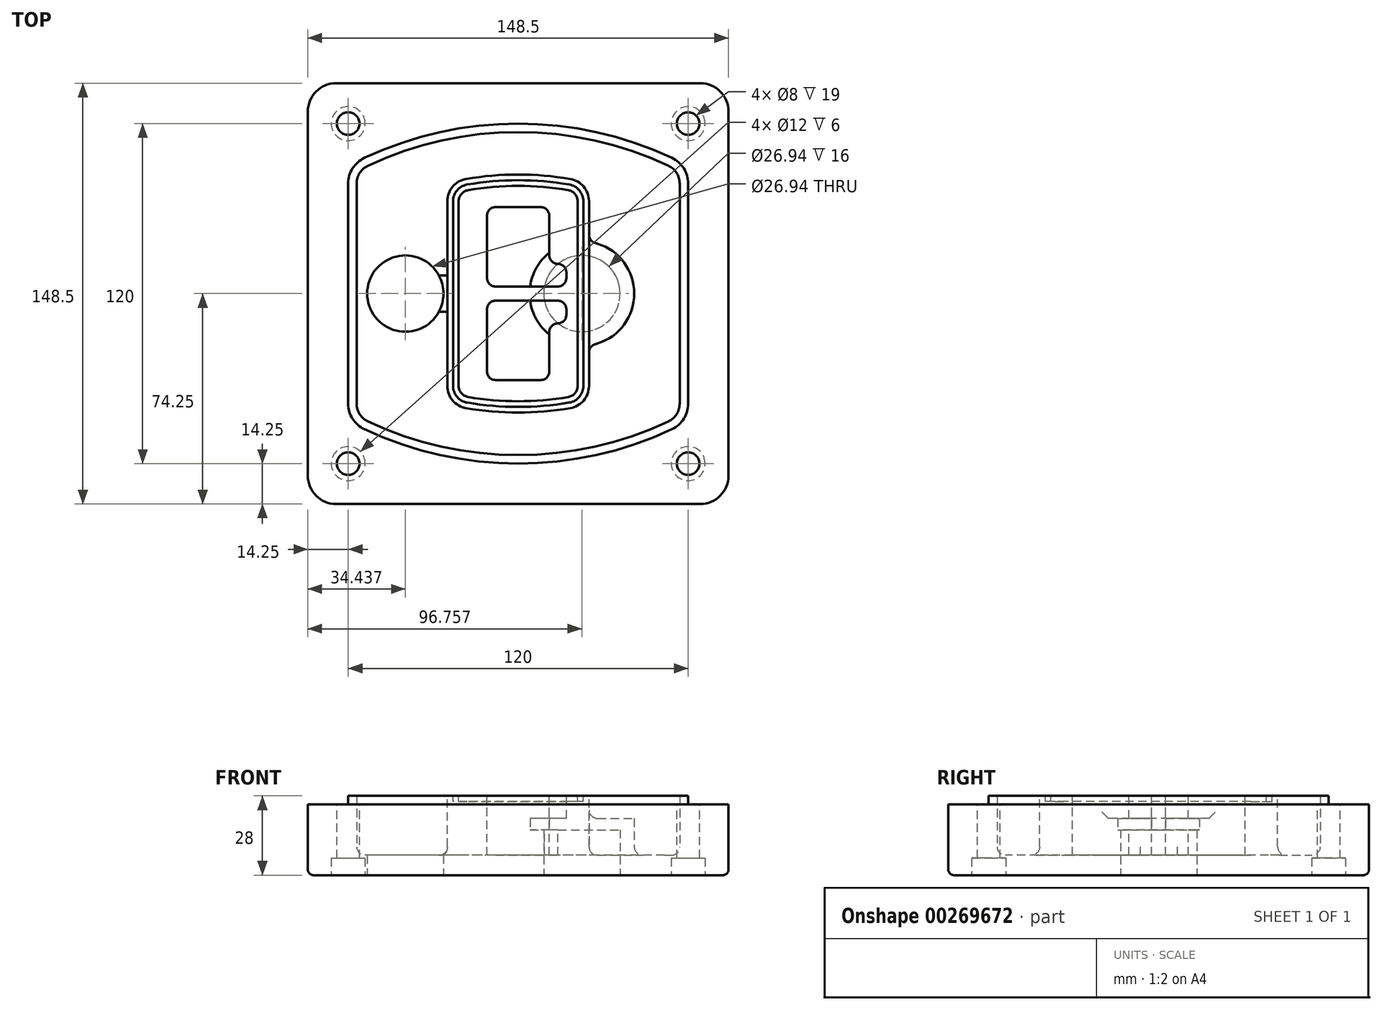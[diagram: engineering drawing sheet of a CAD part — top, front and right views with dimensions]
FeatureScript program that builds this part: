
annotation { "Feature Type Name" : "Feature", "Feature Type Description" : "" }
export const myFeature = defineFeature(function(context is Context, id is Id, definition is map)
    precondition{}
    {
        {
            var Q0;
            Q0=qCreatedBy(makeId("Top.planeOp"),FACE);
            var sketch = newSketch(context, id + "F0", { "sketchPlane" : qUnion([Q0])});
            skPoint(sketch, "E0.rect.middle", {"position": v(0, 0) * mm});
            skLineSegment(sketch, "E1.bottom", {"start": v(-64.25, -74.25) * mm, "end": v(64.25, -74.25) * mm});
            skLineSegment(sketch, "E1.top", {"start": v(-64.25, 74.25) * mm, "end": v(64.25, 74.25) * mm});
            skLineSegment(sketch, "E1.left", {"start": v(-74.25, -64.25) * mm, "end": v(-74.25, 64.25) * mm});
            skLineSegment(sketch, "E1.right", {"start": v(74.25, -64.25) * mm, "end": v(74.25, 64.25) * mm});
            skLineSegment(sketch, "E2", {"start": v(-74.25, 74.25) * mm, "end": v(74.25, -74.25) * mm, "construction": true});
            skLineSegment(sketch, "E3", {"start": v(74.25, 74.25) * mm, "end": v(-74.25, -74.25) * mm, "construction": true});
            skCircle(sketch, "E4", {"center": v(-60, 60) * mm, "radius": 4 * mm});
            skCircle(sketch, "E5", {"center": v(60, 60) * mm, "radius": 4 * mm});
            skCircle(sketch, "E6", {"center": v(60, -60) * mm, "radius": 4 * mm});
            skCircle(sketch, "E7", {"center": v(-60, -60) * mm, "radius": 4 * mm});
            skLineSegment(sketch, "E8", {"start": v(-60, 60) * mm, "end": v(60, 60) * mm, "construction": true});
            skLineSegment(sketch, "E9", {"start": v(60, 60) * mm, "end": v(60, -60) * mm, "construction": true});
            skLineSegment(sketch, "E10", {"start": v(60, -60) * mm, "end": v(-60, -60) * mm, "construction": true});
            skLineSegment(sketch, "E11", {"start": v(-60, -60) * mm, "end": v(-60, 60) * mm, "construction": true});
            skLineSegment(sketch, "E12", {"start": v(-60, 38.83) * mm, "end": v(-60, -38.83) * mm});
            skLineSegment(sketch, "E13", {"start": v(60, 38.83) * mm, "end": v(60, -38.83) * mm});
            skArc(sketch, "E14", {"start": v(54.26, 47.88) * mm, "mid": v(0, 60) * mm, "end": v(-54.26, 47.88) * mm});
            skArc(sketch, "E15", {"start": v(-54.26, -47.88) * mm, "mid": v(0, -60) * mm, "end": v(54.26, -47.88) * mm});
            skLineSegment(sketch, "E16", {"start": v(-60, 0) * mm, "end": v(60, 0) * mm, "construction": true});
            skPoint(sketch, "E17.visualSharp", {"position": v(-60, -45) * mm});
            skArc(sketch, "E17.filletArc", {"start": v(-60, -38.83) * mm, "mid": v(-58.44, -44.2) * mm, "end": v(-54.26, -47.88) * mm});
            skPoint(sketch, "E18.visualSharp", {"position": v(-60, 45) * mm});
            skArc(sketch, "E18.filletArc", {"start": v(-54.26, 47.88) * mm, "mid": v(-58.44, 44.2) * mm, "end": v(-60, 38.83) * mm});
            skPoint(sketch, "E19.visualSharp", {"position": v(60, 45) * mm});
            skArc(sketch, "E19.filletArc", {"start": v(60, 38.83) * mm, "mid": v(58.44, 44.2) * mm, "end": v(54.26, 47.88) * mm});
            skPoint(sketch, "E20.visualSharp", {"position": v(60, -45) * mm});
            skArc(sketch, "E20.filletArc", {"start": v(54.26, -47.88) * mm, "mid": v(58.44, -44.2) * mm, "end": v(60, -38.83) * mm});
            skPoint(sketch, "E21.visualSharp", {"position": v(-74.25, 74.25) * mm});
            skArc(sketch, "E21.filletArc", {"start": v(-64.25, 74.25) * mm, "mid": v(-71.32, 71.32) * mm, "end": v(-74.25, 64.25) * mm});
            skPoint(sketch, "E22.visualSharp", {"position": v(74.25, 74.25) * mm});
            skArc(sketch, "E22.filletArc", {"start": v(74.25, 64.25) * mm, "mid": v(71.32, 71.32) * mm, "end": v(64.25, 74.25) * mm});
            skPoint(sketch, "E23.visualSharp", {"position": v(74.25, -74.25) * mm});
            skArc(sketch, "E23.filletArc", {"start": v(64.25, -74.25) * mm, "mid": v(71.32, -71.32) * mm, "end": v(74.25, -64.25) * mm});
            skPoint(sketch, "E24.visualSharp", {"position": v(-74.25, -74.25) * mm});
            skArc(sketch, "E24.filletArc", {"start": v(-74.25, -64.25) * mm, "mid": v(-71.32, -71.32) * mm, "end": v(-64.25, -74.25) * mm});
            skArc(sketch, "E25.0", {"start": v(57, 38.83) * mm, "mid": v(55.9, 42.58) * mm, "end": v(52.98, 45.17) * mm});
            skLineSegment(sketch, "E25.1", {"start": v(57, 38.83) * mm, "end": v(57, -38.83) * mm});
            skArc(sketch, "E25.2", {"start": v(52.98, -45.17) * mm, "mid": v(55.9, -42.58) * mm, "end": v(57, -38.83) * mm});
            skArc(sketch, "E25.3", {"start": v(-52.98, -45.17) * mm, "mid": v(0, -57) * mm, "end": v(52.98, -45.17) * mm});
            skArc(sketch, "E25.4", {"start": v(-57, -38.83) * mm, "mid": v(-55.9, -42.58) * mm, "end": v(-52.98, -45.17) * mm});
            skArc(sketch, "E25.5", {"start": v(52.98, 45.17) * mm, "mid": v(0, 57) * mm, "end": v(-52.98, 45.17) * mm});
            skLineSegment(sketch, "E25.6", {"start": v(-57, 38.83) * mm, "end": v(-57, -38.83) * mm});
            skArc(sketch, "E25.7", {"start": v(-52.98, 45.17) * mm, "mid": v(-55.9, 42.58) * mm, "end": v(-57, 38.83) * mm});
            skArc(sketch, "E26.0", {"start": v(-55.96, 51.5) * mm, "mid": v(-61.82, 46.33) * mm, "end": v(-64, 38.83) * mm});
            skArc(sketch, "E26.1", {"start": v(55.96, 51.5) * mm, "mid": v(0, 64) * mm, "end": v(-55.96, 51.5) * mm});
            skArc(sketch, "E26.2", {"start": v(64, 38.83) * mm, "mid": v(61.82, 46.33) * mm, "end": v(55.96, 51.5) * mm});
            skLineSegment(sketch, "E26.3", {"start": v(64, 38.83) * mm, "end": v(64, -38.83) * mm});
            skArc(sketch, "E26.4", {"start": v(55.96, -51.5) * mm, "mid": v(61.82, -46.33) * mm, "end": v(64, -38.83) * mm});
            skLineSegment(sketch, "E26.5", {"start": v(-64, 38.83) * mm, "end": v(-64, -38.83) * mm});
            skArc(sketch, "E26.6", {"start": v(-55.96, -51.5) * mm, "mid": v(0, -64) * mm, "end": v(55.96, -51.5) * mm});
            skArc(sketch, "E26.7", {"start": v(-64, -38.83) * mm, "mid": v(-61.82, -46.33) * mm, "end": v(-55.96, -51.5) * mm});
            skSolve(sketch);
        }
        {
            var Q0;
            Q0=makeQuery(id+"F0.imprint","IMPRINT",FACE,{"disambiguationData":[TD([[makeQuery(id+"F0.imprint","IMPRINT",EDGE,{"derivedFrom":sQuery(id+"F0.wireOp",EDGE,"E1.bottom")}),1.0]])]});
            var Q1;
            Q1=makeQuery(id+"F0.imprint","IMPRINT",FACE,{"disambiguationData":[TD([[makeQuery(id+"F0.imprint","IMPRINT",EDGE,{"derivedFrom":sQuery(id+"F0.wireOp",EDGE,"E12")}),1.0]])]});
            var Q2;
            Q2=makeQuery(id+"F0.imprint","IMPRINT",FACE,{"disambiguationData":[TD([[makeQuery(id+"F0.imprint","IMPRINT",EDGE,{"derivedFrom":sQuery(id+"F0.wireOp",EDGE,"E25.0")}),1.0]])]});
            var Q3;
            Q3=makeQuery(id+"F0.imprint","IMPRINT",FACE,{"disambiguationData":[TD([[makeQuery(id+"F0.imprint","IMPRINT",EDGE,{"derivedFrom":sQuery(id+"F0.wireOp",EDGE,"E12")}),-1.0]])]});
            extrude(context, id + "F1", {"entities" : qUnion([Q0, Q1, Q2, Q3]), "oppositeDirection" : true, "depth" : 25 * mm});
        }
        {
            var Q0;
            Q0=makeQuery(id+"F0.imprint","IMPRINT",FACE,{"disambiguationData":[TD([[makeQuery(id+"F0.imprint","IMPRINT",EDGE,{"derivedFrom":sQuery(id+"F0.wireOp",EDGE,"E12")}),1.0]])]});
            extrude(context, id + "F2", {"entities" : qUnion([Q0]), "operationType" : NewBodyOperationType.ADD, "depth" : 3 * mm});
        }
        {
            var Q0;
            Q0=makeQuery(id+"F0.imprint","IMPRINT",FACE,{"disambiguationData":[TD([[makeQuery(id+"F0.imprint","IMPRINT",EDGE,{"derivedFrom":sQuery(id+"F0.wireOp",EDGE,"E25.0")}),1.0]])]});
            extrude(context, id + "F3", {"entities" : qUnion([Q0]), "operationType" : NewBodyOperationType.REMOVE, "oppositeDirection" : true, "depth" : 18 * mm});
        }
        {
            var Q0;
            Q0=makeQuery(id+"F2.opExtrude","CAP_FACE",FACE,{"disambiguationData":[OSD([sQuery(id+"F0.wireOp",EDGE,"E12"),sQuery(id+"F0.wireOp",EDGE,"E13"),sQuery(id+"F0.wireOp",EDGE,"E14"),sQuery(id+"F0.wireOp",EDGE,"E15"),sQuery(id+"F0.wireOp",EDGE,"E17.filletArc"),sQuery(id+"F0.wireOp",EDGE,"E18.filletArc"),sQuery(id+"F0.wireOp",EDGE,"E19.filletArc"),sQuery(id+"F0.wireOp",EDGE,"E20.filletArc"),sQuery(id+"F0.wireOp",EDGE,"E25.0"),sQuery(id+"F0.wireOp",EDGE,"E25.1"),sQuery(id+"F0.wireOp",EDGE,"E25.2"),sQuery(id+"F0.wireOp",EDGE,"E25.3"),sQuery(id+"F0.wireOp",EDGE,"E25.4"),sQuery(id+"F0.wireOp",EDGE,"E25.5"),sQuery(id+"F0.wireOp",EDGE,"E25.6"),sQuery(id+"F0.wireOp",EDGE,"E25.7")])],"isStart":false});
            var sketch = newSketch(context, id + "F4", { "sketchPlane" : qUnion([Q0])});
            skArc(sketch, "E27.0", {"start": v(-18.34, -40.45) * mm, "mid": v(0, -42) * mm, "end": v(18.34, -40.45) * mm});
            skArc(sketch, "E28.0", {"start": v(18.34, 40.45) * mm, "mid": v(0, 42) * mm, "end": v(-18.34, 40.45) * mm});
            skLineSegment(sketch, "E29", {"start": v(-25, 32.57) * mm, "end": v(-25, -32.57) * mm});
            skLineSegment(sketch, "E30", {"start": v(25, 32.57) * mm, "end": v(25, -32.57) * mm});
            skLineSegment(sketch, "E31", {"start": v(-25, 39.1) * mm, "end": v(25, 39.1) * mm, "construction": true});
            skLineSegment(sketch, "E32", {"start": v(-25, -39.1) * mm, "end": v(25, -39.1) * mm, "construction": true});
            skPoint(sketch, "E33.visualSharp", {"position": v(-25, 39.1) * mm});
            skArc(sketch, "E33.filletArc", {"start": v(-18.34, 40.45) * mm, "mid": v(-23.11, 37.73) * mm, "end": v(-25, 32.57) * mm});
            skPoint(sketch, "E34.visualSharp", {"position": v(25, 39.1) * mm});
            skArc(sketch, "E34.filletArc", {"start": v(25, 32.57) * mm, "mid": v(23.11, 37.73) * mm, "end": v(18.34, 40.45) * mm});
            skPoint(sketch, "E35.visualSharp", {"position": v(25, -39.1) * mm});
            skArc(sketch, "E35.filletArc", {"start": v(18.34, -40.45) * mm, "mid": v(23.11, -37.73) * mm, "end": v(25, -32.57) * mm});
            skPoint(sketch, "E36.visualSharp", {"position": v(-25, -39.1) * mm});
            skArc(sketch, "E36.filletArc", {"start": v(-25, -32.57) * mm, "mid": v(-23.11, -37.73) * mm, "end": v(-18.34, -40.45) * mm});
            skArc(sketch, "E37.0", {"start": v(52.98, 45.17) * mm, "mid": v(0, 57) * mm, "end": v(-52.98, 45.17) * mm});
            skArc(sketch, "E37.1", {"start": v(-52.98, 45.17) * mm, "mid": v(-55.9, 42.58) * mm, "end": v(-57, 38.83) * mm});
            skLineSegment(sketch, "E37.2", {"start": v(-57, 38.83) * mm, "end": v(-57, -38.83) * mm});
            skArc(sketch, "E37.3", {"start": v(-57, -38.83) * mm, "mid": v(-55.9, -42.58) * mm, "end": v(-52.98, -45.17) * mm});
            skArc(sketch, "E37.4", {"start": v(-52.98, -45.17) * mm, "mid": v(0, -57) * mm, "end": v(52.98, -45.17) * mm});
            skArc(sketch, "E37.5", {"start": v(52.98, -45.17) * mm, "mid": v(55.9, -42.58) * mm, "end": v(57, -38.83) * mm});
            skLineSegment(sketch, "E37.6", {"start": v(57, 38.83) * mm, "end": v(57, -38.83) * mm});
            skArc(sketch, "E37.7", {"start": v(57, 38.83) * mm, "mid": v(55.9, 42.58) * mm, "end": v(52.98, 45.17) * mm});
            skLineSegment(sketch, "E38.0", {"start": v(23, 32.57) * mm, "end": v(23, -32.57) * mm});
            skArc(sketch, "E38.1", {"start": v(18, -38.48) * mm, "mid": v(21.58, -36.44) * mm, "end": v(23, -32.57) * mm});
            skArc(sketch, "E38.2", {"start": v(-18, -38.48) * mm, "mid": v(0, -40) * mm, "end": v(18, -38.48) * mm});
            skArc(sketch, "E38.3", {"start": v(-23, -32.57) * mm, "mid": v(-21.58, -36.44) * mm, "end": v(-18, -38.48) * mm});
            skLineSegment(sketch, "E38.4", {"start": v(-23, 32.57) * mm, "end": v(-23, -32.57) * mm});
            skArc(sketch, "E38.5", {"start": v(23, 32.57) * mm, "mid": v(21.58, 36.44) * mm, "end": v(18, 38.48) * mm});
            skArc(sketch, "E38.6", {"start": v(-18, 38.48) * mm, "mid": v(-21.58, 36.44) * mm, "end": v(-23, 32.57) * mm});
            skArc(sketch, "E38.7", {"start": v(18, 38.48) * mm, "mid": v(0, 40) * mm, "end": v(-18, 38.48) * mm});
            skArc(sketch, "E39.0", {"start": v(21, 32.57) * mm, "mid": v(20.06, 35.15) * mm, "end": v(17.67, 36.5) * mm});
            skLineSegment(sketch, "E39.1", {"start": v(21, 32.57) * mm, "end": v(21, -32.57) * mm});
            skArc(sketch, "E39.2", {"start": v(17.67, -36.5) * mm, "mid": v(20.06, -35.15) * mm, "end": v(21, -32.57) * mm});
            skArc(sketch, "E39.3", {"start": v(-17.67, -36.5) * mm, "mid": v(0, -38) * mm, "end": v(17.67, -36.5) * mm});
            skArc(sketch, "E39.4", {"start": v(-21, -32.57) * mm, "mid": v(-20.06, -35.15) * mm, "end": v(-17.67, -36.5) * mm});
            skArc(sketch, "E39.5", {"start": v(17.67, 36.5) * mm, "mid": v(0, 38) * mm, "end": v(-17.67, 36.5) * mm});
            skLineSegment(sketch, "E39.6", {"start": v(-21, 32.57) * mm, "end": v(-21, -32.57) * mm});
            skArc(sketch, "E39.7", {"start": v(-17.67, 36.5) * mm, "mid": v(-20.06, 35.15) * mm, "end": v(-21, 32.57) * mm});
            skLineSegment(sketch, "E40", {"start": v(-25, 0) * mm, "end": v(25, 0) * mm, "construction": true});
            skLineSegment(sketch, "E41", {"start": v(-11, 5.5) * mm, "end": v(-11, 27.5) * mm});
            skLineSegment(sketch, "E42", {"start": v(-8, 30.5) * mm, "end": v(8, 30.5) * mm});
            skLineSegment(sketch, "E43", {"start": v(11, 27.5) * mm, "end": v(11, 13.5) * mm});
            skLineSegment(sketch, "E44", {"start": v(14, 10.5) * mm, "end": v(14, 10.5) * mm});
            skLineSegment(sketch, "E45", {"start": v(17, 7.5) * mm, "end": v(17, 5.5) * mm});
            skLineSegment(sketch, "E46", {"start": v(14, 2.5) * mm, "end": v(-8, 2.5) * mm});
            skPoint(sketch, "E47.visualSharp", {"position": v(-11, 30.5) * mm});
            skArc(sketch, "E47.filletArc", {"start": v(-8, 30.5) * mm, "mid": v(-10.12, 29.62) * mm, "end": v(-11, 27.5) * mm});
            skPoint(sketch, "E48.visualSharp", {"position": v(11, 30.5) * mm});
            skArc(sketch, "E48.filletArc", {"start": v(11, 27.5) * mm, "mid": v(10.12, 29.62) * mm, "end": v(8, 30.5) * mm});
            skPoint(sketch, "E49.visualSharp", {"position": v(11, 10.5) * mm});
            skArc(sketch, "E49.filletArc", {"start": v(11, 13.5) * mm, "mid": v(11.88, 11.38) * mm, "end": v(14, 10.5) * mm});
            skPoint(sketch, "E50.visualSharp", {"position": v(17, 10.5) * mm});
            skArc(sketch, "E50.filletArc", {"start": v(17, 7.5) * mm, "mid": v(16.12, 9.62) * mm, "end": v(14, 10.5) * mm});
            skPoint(sketch, "E51.visualSharp", {"position": v(17, 2.5) * mm});
            skArc(sketch, "E51.filletArc", {"start": v(14, 2.5) * mm, "mid": v(16.12, 3.38) * mm, "end": v(17, 5.5) * mm});
            skPoint(sketch, "E52.visualSharp", {"position": v(-11, 2.5) * mm});
            skArc(sketch, "E52.filletArc", {"start": v(-11, 5.5) * mm, "mid": v(-10.12, 3.38) * mm, "end": v(-8, 2.5) * mm});
            skLineSegment(sketch, "E53.0.MirrorCS", {"start": v(14, -2.5) * mm, "end": v(-8, -2.5) * mm});
            skArc(sketch, "E54.0.MirrorCS", {"start": v(-11, -5.5) * mm, "mid": v(-10.12, -3.38) * mm, "end": v(-8, -2.5) * mm});
            skLineSegment(sketch, "E55.0.MirrorCS", {"start": v(-11, -5.5) * mm, "end": v(-11, -27.5) * mm});
            skArc(sketch, "E56.0.MirrorCS", {"start": v(-8, -30.5) * mm, "mid": v(-10.12, -29.62) * mm, "end": v(-11, -27.5) * mm});
            skLineSegment(sketch, "E57.0.MirrorCS", {"start": v(-8, -30.5) * mm, "end": v(8, -30.5) * mm});
            skArc(sketch, "E58.0.MirrorCS", {"start": v(11, -27.5) * mm, "mid": v(10.12, -29.62) * mm, "end": v(8, -30.5) * mm});
            skLineSegment(sketch, "E59.0.MirrorCS", {"start": v(11, -27.5) * mm, "end": v(11, -13.5) * mm});
            skArc(sketch, "E60.0.MirrorCS", {"start": v(11, -13.5) * mm, "mid": v(11.88, -11.38) * mm, "end": v(14, -10.5) * mm});
            skArc(sketch, "E61.0.MirrorCS", {"start": v(17, -7.5) * mm, "mid": v(16.12, -9.62) * mm, "end": v(14, -10.5) * mm});
            skLineSegment(sketch, "E62.0.MirrorCS", {"start": v(17, -7.5) * mm, "end": v(17, -5.5) * mm});
            skArc(sketch, "E63.0.MirrorCS", {"start": v(14, -2.5) * mm, "mid": v(16.12, -3.38) * mm, "end": v(17, -5.5) * mm});
            skSolve(sketch);
        }
        {
            var Q0;
            Q0=makeQuery(id+"F4.imprint","IMPRINT",FACE,{"disambiguationData":[TD([[makeQuery(id+"F4.imprint","IMPRINT",EDGE,{"derivedFrom":sQuery(id+"F4.wireOp",EDGE,"E27.0")}),1.0]])]});
            var Q1;
            Q1=makeQuery(id+"F4.imprint","IMPRINT",FACE,{"disambiguationData":[TD([[makeQuery(id+"F4.imprint","IMPRINT",EDGE,{"derivedFrom":sQuery(id+"F4.wireOp",EDGE,"E38.0")}),-1.0]])]});
            var Q2;
            Q2=makeQuery(id+"F4.imprint","IMPRINT",FACE,{"disambiguationData":[TD([[makeQuery(id+"F4.imprint","IMPRINT",EDGE,{"derivedFrom":sQuery(id+"F4.wireOp",EDGE,"E39.0")}),1.0]])]});
            extrude(context, id + "F5", {"entities" : qUnion([Q0, Q1, Q2]), "operationType" : NewBodyOperationType.ADD, "endBound" : BoundingType.UP_TO_NEXT, "oppositeDirection" : true, "depth" : 25 * mm});
        }
        {
            var Q0;
            Q0=makeQuery(id+"F4.imprint","IMPRINT",FACE,{"disambiguationData":[TD([[makeQuery(id+"F4.imprint","IMPRINT",EDGE,{"derivedFrom":sQuery(id+"F4.wireOp",EDGE,"E38.0")}),-1.0]])]});
            extrude(context, id + "F6", {"entities" : qUnion([Q0]), "operationType" : NewBodyOperationType.REMOVE, "oppositeDirection" : true, "depth" : 2 * mm});
        }
        {
            var Q0;
            Q0=makeQuery(id+"F1.opExtrude","CAP_FACE",FACE,{"disambiguationData":[OSD([sQuery(id+"F0.wireOp",EDGE,"E1.bottom"),sQuery(id+"F0.wireOp",EDGE,"E1.top"),sQuery(id+"F0.wireOp",EDGE,"E1.left"),sQuery(id+"F0.wireOp",EDGE,"E1.right"),sQuery(id+"F0.wireOp",EDGE,"E4"),sQuery(id+"F0.wireOp",EDGE,"E5"),sQuery(id+"F0.wireOp",EDGE,"E6"),sQuery(id+"F0.wireOp",EDGE,"E7"),sQuery(id+"F0.wireOp",EDGE,"E21.filletArc"),sQuery(id+"F0.wireOp",EDGE,"E22.filletArc"),sQuery(id+"F0.wireOp",EDGE,"E23.filletArc"),sQuery(id+"F0.wireOp",EDGE,"E24.filletArc")])],"isStart":false});
            var sketch = newSketch(context, id + "F7", { "sketchPlane" : qUnion([Q0])});
            skCircle(sketch, "E64", {"center": v(22.5, 0) * mm, "radius": 13.47 * mm});
            skCircle(sketch, "E65", {"center": v(-39.81, 0) * mm, "radius": 13.47 * mm});
            skLineSegment(sketch, "E66", {"start": v(74.25, 0) * mm, "end": v(-74.25, 0) * mm});
            skCircle(sketch, "E67", {"center": v(22.5, 0) * mm, "radius": 18.47 * mm});
            skCircle(sketch, "E68", {"center": v(60, -60) * mm, "radius": 6 * mm});
            skCircle(sketch, "E69", {"center": v(-60, -60) * mm, "radius": 6 * mm});
            skCircle(sketch, "E70", {"center": v(-60, 60) * mm, "radius": 6 * mm});
            skCircle(sketch, "E71", {"center": v(60, 60) * mm, "radius": 6 * mm});
            skSolve(sketch);
        }
        {
            var Q0;
            {var subQ1=sQuery(id+"F7.wireOp",EDGE,"E66");var subQ4=sQuery(id+"F7.wireOp",EDGE,"E64");var subQ6=makeQuery(id+"F7.imprint","INTERSECT",VERTEX,{"disambiguationData":[OD(0.0)],"derivedFrom":[subQ4,subQ1]});Q0=makeQuery(id+"F7.imprint","IMPRINT",FACE,{"disambiguationData":[TD([[makeQuery(id+"F7.imprint","IMPRINT",EDGE,{"disambiguationData":[TD([[subQ6,-1.0]])],"derivedFrom":subQ4}),-1.0]])]});}
            var Q1;
            {var subQ0=sQuery(id+"F7.wireOp",EDGE,"E66");var subQ1=sQuery(id+"F7.wireOp",EDGE,"E64");var subQ3=makeQuery(id+"F7.imprint","INTERSECT",VERTEX,{"disambiguationData":[OD(0.0)],"derivedFrom":[subQ1,subQ0]});Q1=makeQuery(id+"F7.imprint","IMPRINT",FACE,{"disambiguationData":[TD([[makeQuery(id+"F7.imprint","IMPRINT",EDGE,{"disambiguationData":[TD([[subQ3,-1.0]])],"derivedFrom":subQ1}),1.0]])]});}
            var Q2;
            {var subQ0=sQuery(id+"F7.wireOp",EDGE,"E66");var subQ1=sQuery(id+"F7.wireOp",EDGE,"E64");var subQ3=makeQuery(id+"F7.imprint","INTERSECT",VERTEX,{"disambiguationData":[OD(0.0)],"derivedFrom":[subQ1,subQ0]});Q2=makeQuery(id+"F7.imprint","IMPRINT",FACE,{"disambiguationData":[TD([[makeQuery(id+"F7.imprint","IMPRINT",EDGE,{"disambiguationData":[TD([[subQ3,1.0]])],"derivedFrom":subQ1}),1.0]])]});}
            var Q3;
            {var subQ1=sQuery(id+"F7.wireOp",EDGE,"E66");var subQ4=sQuery(id+"F7.wireOp",EDGE,"E64");var subQ6=makeQuery(id+"F7.imprint","INTERSECT",VERTEX,{"disambiguationData":[OD(0.0)],"derivedFrom":[subQ4,subQ1]});Q3=makeQuery(id+"F7.imprint","IMPRINT",FACE,{"disambiguationData":[TD([[makeQuery(id+"F7.imprint","IMPRINT",EDGE,{"disambiguationData":[TD([[subQ6,1.0]])],"derivedFrom":subQ4}),-1.0]])]});}
            extrude(context, id + "F8", {"entities" : qUnion([Q0, Q1, Q2, Q3]), "operationType" : NewBodyOperationType.ADD, "oppositeDirection" : true, "depth" : 20 * mm});
        }
        {
            var Q0;
            {var subQ0=sQuery(id+"F7.wireOp",EDGE,"E66");var subQ1=sQuery(id+"F7.wireOp",EDGE,"E64");var subQ3=makeQuery(id+"F7.imprint","INTERSECT",VERTEX,{"disambiguationData":[OD(0.0)],"derivedFrom":[subQ1,subQ0]});Q0=makeQuery(id+"F7.imprint","IMPRINT",FACE,{"disambiguationData":[TD([[makeQuery(id+"F7.imprint","IMPRINT",EDGE,{"disambiguationData":[TD([[subQ3,-1.0]])],"derivedFrom":subQ1}),1.0]])]});}
            var Q1;
            {var subQ0=sQuery(id+"F7.wireOp",EDGE,"E66");var subQ1=sQuery(id+"F7.wireOp",EDGE,"E64");var subQ3=makeQuery(id+"F7.imprint","INTERSECT",VERTEX,{"disambiguationData":[OD(0.0)],"derivedFrom":[subQ1,subQ0]});Q1=makeQuery(id+"F7.imprint","IMPRINT",FACE,{"disambiguationData":[TD([[makeQuery(id+"F7.imprint","IMPRINT",EDGE,{"disambiguationData":[TD([[subQ3,1.0]])],"derivedFrom":subQ1}),1.0]])]});}
            extrude(context, id + "F9", {"entities" : qUnion([Q0, Q1]), "operationType" : NewBodyOperationType.REMOVE, "oppositeDirection" : true, "depth" : 16 * mm});
        }
        {
            var Q0;
            {var subQ0=sQuery(id+"F7.wireOp",EDGE,"E66");var subQ1=sQuery(id+"F7.wireOp",EDGE,"E65");var subQ3=makeQuery(id+"F7.imprint","INTERSECT",VERTEX,{"disambiguationData":[OD(0.0)],"derivedFrom":[subQ1,subQ0]});Q0=makeQuery(id+"F7.imprint","IMPRINT",FACE,{"disambiguationData":[TD([[makeQuery(id+"F7.imprint","IMPRINT",EDGE,{"disambiguationData":[TD([[subQ3,-1.0]])],"derivedFrom":subQ1}),1.0]])]});}
            var Q1;
            {var subQ0=sQuery(id+"F7.wireOp",EDGE,"E66");var subQ1=sQuery(id+"F7.wireOp",EDGE,"E65");var subQ3=makeQuery(id+"F7.imprint","INTERSECT",VERTEX,{"disambiguationData":[OD(0.0)],"derivedFrom":[subQ1,subQ0]});Q1=makeQuery(id+"F7.imprint","IMPRINT",FACE,{"disambiguationData":[TD([[makeQuery(id+"F7.imprint","IMPRINT",EDGE,{"disambiguationData":[TD([[subQ3,1.0]])],"derivedFrom":subQ1}),1.0]])]});}
            extrude(context, id + "F10", {"entities" : qUnion([Q0, Q1]), "operationType" : NewBodyOperationType.REMOVE, "oppositeDirection" : true, "depth" : 25 * mm});
        }
        {
            var Q0;
            Q0=makeQuery(id+"F7.imprint","IMPRINT",FACE,{"disambiguationData":[TD([[makeQuery(id+"F7.imprint","IMPRINT",EDGE,{"derivedFrom":sQuery(id+"F7.wireOp",EDGE,"E68")}),1.0]])]});
            var Q1;
            Q1=makeQuery(id+"F7.imprint","IMPRINT",FACE,{"disambiguationData":[TD([[makeQuery(id+"F7.imprint","IMPRINT",EDGE,{"derivedFrom":makeQuery(id+"F1.opExtrude","CAP_EDGE",EDGE,{"disambiguationData":[OSD([sQuery(id+"F0.wireOp",EDGE,"E5")])],"isStart":false})}),-1.0]])]});
            var Q2;
            Q2=makeQuery(id+"F7.imprint","IMPRINT",FACE,{"disambiguationData":[TD([[makeQuery(id+"F7.imprint","IMPRINT",EDGE,{"derivedFrom":sQuery(id+"F7.wireOp",EDGE,"E69")}),1.0]])]});
            var Q3;
            Q3=makeQuery(id+"F7.imprint","IMPRINT",FACE,{"disambiguationData":[TD([[makeQuery(id+"F7.imprint","IMPRINT",EDGE,{"derivedFrom":makeQuery(id+"F1.opExtrude","CAP_EDGE",EDGE,{"disambiguationData":[OSD([sQuery(id+"F0.wireOp",EDGE,"E4")])],"isStart":false})}),-1.0]])]});
            var Q4;
            Q4=makeQuery(id+"F7.imprint","IMPRINT",FACE,{"disambiguationData":[TD([[makeQuery(id+"F7.imprint","IMPRINT",EDGE,{"derivedFrom":sQuery(id+"F7.wireOp",EDGE,"E70")}),1.0]])]});
            var Q5;
            Q5=makeQuery(id+"F7.imprint","IMPRINT",FACE,{"disambiguationData":[TD([[makeQuery(id+"F7.imprint","IMPRINT",EDGE,{"derivedFrom":makeQuery(id+"F1.opExtrude","CAP_EDGE",EDGE,{"disambiguationData":[OSD([sQuery(id+"F0.wireOp",EDGE,"E7")])],"isStart":false})}),-1.0]])]});
            var Q6;
            Q6=makeQuery(id+"F7.imprint","IMPRINT",FACE,{"disambiguationData":[TD([[makeQuery(id+"F7.imprint","IMPRINT",EDGE,{"derivedFrom":sQuery(id+"F7.wireOp",EDGE,"E71")}),1.0]])]});
            var Q7;
            Q7=makeQuery(id+"F7.imprint","IMPRINT",FACE,{"disambiguationData":[TD([[makeQuery(id+"F7.imprint","IMPRINT",EDGE,{"derivedFrom":makeQuery(id+"F1.opExtrude","CAP_EDGE",EDGE,{"disambiguationData":[OSD([sQuery(id+"F0.wireOp",EDGE,"E6")])],"isStart":false})}),-1.0]])]});
            extrude(context, id + "F11", {"entities" : qUnion([Q0, Q1, Q2, Q3, Q4, Q5, Q6, Q7]), "operationType" : NewBodyOperationType.REMOVE, "oppositeDirection" : true, "depth" : 6 * mm});
        }
        {
            var Q0;
            Q0=makeQuery(id+"F9.boolean.opBoolean","COPY",FACE,{"derivedFrom":makeQuery(id+"F9.opExtrude","CAP_FACE",FACE,{"disambiguationData":[OSD([sQuery(id+"F7.wireOp",EDGE,"E64")])],"isStart":false})});
            var sketch = newSketch(context, id + "F12", { "sketchPlane" : qUnion([Q0])});
            skArc(sketch, "E72.0", {"start": v(11, 14.45) * mm, "mid": v(6.45, 9.13) * mm, "end": v(4.2, 2.5) * mm});
            skArc(sketch, "E72.1", {"start": v(4.2, -2.5) * mm, "mid": v(6.45, -9.13) * mm, "end": v(11, -14.45) * mm});
            skLineSegment(sketch, "E73", {"start": v(4.2, -2.5) * mm, "end": v(14, -2.5) * mm});
            skLineSegment(sketch, "E74.0", {"start": v(14, 2.5) * mm, "end": v(4.2, 2.5) * mm});
            skArc(sketch, "E74.1", {"start": v(14, 2.5) * mm, "mid": v(16.12, 3.38) * mm, "end": v(17, 5.5) * mm});
            skLineSegment(sketch, "E74.2", {"start": v(17, 7.5) * mm, "end": v(17, 5.5) * mm});
            skArc(sketch, "E74.3", {"start": v(17, 7.5) * mm, "mid": v(16.12, 9.62) * mm, "end": v(14, 10.5) * mm});
            skArc(sketch, "E74.4", {"start": v(11, 13.5) * mm, "mid": v(11.88, 11.38) * mm, "end": v(14, 10.5) * mm});
            skLineSegment(sketch, "E74.5", {"start": v(11, 14.45) * mm, "end": v(11, 13.5) * mm});
            skLineSegment(sketch, "E74.7", {"start": v(14, -2.5) * mm, "end": v(4.2, -2.5) * mm});
            skArc(sketch, "E74.8", {"start": v(14, -2.5) * mm, "mid": v(16.12, -3.38) * mm, "end": v(17, -5.5) * mm});
            skLineSegment(sketch, "E74.9", {"start": v(17, -7.5) * mm, "end": v(17, -5.5) * mm});
            skArc(sketch, "E74.10", {"start": v(17, -7.5) * mm, "mid": v(16.12, -9.62) * mm, "end": v(14, -10.5) * mm});
            skArc(sketch, "E74.11", {"start": v(11, -13.5) * mm, "mid": v(11.88, -11.38) * mm, "end": v(14, -10.5) * mm});
            skLineSegment(sketch, "E74.12", {"start": v(11, -14.45) * mm, "end": v(11, -13.5) * mm});
            skPoint(sketch, "E75.orphan", {"position": v(11, -27.5) * mm});
            skPoint(sketch, "E76.orphan", {"position": v(-8, -2.5) * mm});
            skPoint(sketch, "E77.orphan", {"position": v(-8, 2.5) * mm});
            skPoint(sketch, "E78.orphan", {"position": v(11, 27.5) * mm});
            skSolve(sketch);
        }
        {
            var Q0;
            {var subQ7=sQuery(id+"F12.wireOp",EDGE,"E72.0");var subQ14=sQuery(id+"F12.wireOp",EDGE,"E72.1");var subQ16=sQuery(id+"F12.wireOp",EDGE,"E74.1");var subQ18=sQuery(id+"F12.wireOp",EDGE,"E74.8");Q0=qUnion([makeQuery(id+"F12.imprint","IMPRINT",FACE,{"disambiguationData":[TD([[makeQuery(id+"F12.imprint","IMPRINT",EDGE,{"derivedFrom":subQ7}),1.0]])]}),makeQuery(id+"F12.imprint","IMPRINT",FACE,{"disambiguationData":[TD([[makeQuery(id+"F12.imprint","IMPRINT",EDGE,{"derivedFrom":subQ14}),1.0]])]}),makeQuery(id+"F12.imprint","IMPRINT",FACE,{"disambiguationData":[TD([[makeQuery(id+"F12.imprint","IMPRINT",EDGE,{"derivedFrom":subQ16}),1.0]])]}),makeQuery(id+"F12.imprint","IMPRINT",FACE,{"disambiguationData":[TD([[makeQuery(id+"F12.imprint","IMPRINT",EDGE,{"derivedFrom":subQ18}),-1.0]])]})]);}
            var Q1;
            Q1=makeQuery(id+"F5.boolean.opBoolean","SPLIT",FACE,{"disambiguationData":[TD([makeQuery(id+"F5.opExtrude","SWEPT_FACE",FACE,{"disambiguationData":[OSD([sQuery(id+"F4.wireOp",EDGE,"E41")])]})])],"derivedFrom":makeQuery(id+"F3.boolean.opBoolean","COPY",FACE,{"derivedFrom":makeQuery(id+"F3.opExtrude","CAP_FACE",FACE,{"disambiguationData":[OSD([sQuery(id+"F0.wireOp",EDGE,"E25.0"),sQuery(id+"F0.wireOp",EDGE,"E25.1"),sQuery(id+"F0.wireOp",EDGE,"E25.2"),sQuery(id+"F0.wireOp",EDGE,"E25.3"),sQuery(id+"F0.wireOp",EDGE,"E25.4"),sQuery(id+"F0.wireOp",EDGE,"E25.5"),sQuery(id+"F0.wireOp",EDGE,"E25.6"),sQuery(id+"F0.wireOp",EDGE,"E25.7")])],"isStart":false})})});
            extrude(context, id + "F13", {"entities" : qUnion([Q0]), "operationType" : NewBodyOperationType.REMOVE, "endBound" : BoundingType.UP_TO_SURFACE, "endBoundEntityFace" : qUnion([Q1]), "depth" : 25 * mm});
        }
        {
            var Q0;
            Q0=makeQuery(id+"F3.boolean.opBoolean","COPY",EDGE,{"derivedFrom":makeQuery(id+"F3.opExtrude","CAP_EDGE",EDGE,{"disambiguationData":[OSD([sQuery(id+"F0.wireOp",EDGE,"E25.6")])],"isStart":false})});
            var Q1;
            Q1=makeQuery(id+"F8.boolean.opBoolean","INTERSECT",EDGE,{"derivedFrom":[makeQuery(id+"F5.opExtrude","SWEPT_FACE",FACE,{"disambiguationData":[OSD([sQuery(id+"F4.wireOp",EDGE,"E30")])]}),makeQuery(id+"F8.opExtrude","CAP_FACE",FACE,{"disambiguationData":[OSD([sQuery(id+"F7.wireOp",EDGE,"E67")])],"isStart":false})]});
            var Q2;
            Q2=makeQuery(id+"F8.boolean.opBoolean","INTERSECT",EDGE,{"disambiguationData":[OD(1.0)],"derivedFrom":[makeQuery(id+"F5.opExtrude","SWEPT_FACE",FACE,{"disambiguationData":[OSD([sQuery(id+"F4.wireOp",EDGE,"E30")])]}),makeQuery(id+"F8.opExtrude","SWEPT_FACE",FACE,{"disambiguationData":[OSD([sQuery(id+"F7.wireOp",EDGE,"E67")])]})]});
            var Q3;
            {var subQ0=sQuery(id+"F4.wireOp",EDGE,"E30");Q3=makeQuery(id+"F8.boolean.opBoolean","SPLIT",EDGE,{"disambiguationData":[TD([makeQuery(id+"F5.opExtrude","SWEPT_FACE",FACE,{"disambiguationData":[OSD([sQuery(id+"F4.wireOp",EDGE,"E35.filletArc")])]})])],"derivedFrom":makeQuery(id+"F5.opExtrude","CAP_EDGE",EDGE,{"disambiguationData":[OSD([subQ0])],"isStart":false})});}
            var Q4;
            {var subQ0=sQuery(id+"F0.wireOp",EDGE,"E25.7");var subQ1=sQuery(id+"F0.wireOp",EDGE,"E25.1");var subQ2=sQuery(id+"F0.wireOp",EDGE,"E25.6");var subQ3=sQuery(id+"F0.wireOp",EDGE,"E25.5");var subQ4=sQuery(id+"F0.wireOp",EDGE,"E25.4");var subQ5=sQuery(id+"F0.wireOp",EDGE,"E25.0");var subQ6=sQuery(id+"F0.wireOp",EDGE,"E25.2");var subQ7=sQuery(id+"F0.wireOp",EDGE,"E25.3");Q4=makeQuery(id+"F8.boolean.opBoolean","INTERSECT",EDGE,{"derivedFrom":[makeQuery(id+"F5.boolean.opBoolean","SPLIT",FACE,{"disambiguationData":[TD([makeQuery(id+"F2.opExtrude","SWEPT_FACE",FACE,{"disambiguationData":[OSD([subQ5])]})])],"derivedFrom":makeQuery(id+"F3.boolean.opBoolean","COPY",FACE,{"derivedFrom":makeQuery(id+"F3.opExtrude","CAP_FACE",FACE,{"disambiguationData":[OSD([subQ5,subQ1,subQ6,subQ7,subQ4,subQ3,subQ2,subQ0])],"isStart":false})})}),makeQuery(id+"F8.opExtrude","SWEPT_FACE",FACE,{"disambiguationData":[OSD([sQuery(id+"F7.wireOp",EDGE,"E67")])]})]});}
            var Q5;
            Q5=makeQuery(id+"F8.boolean.opBoolean","INTERSECT",EDGE,{"disambiguationData":[OD(0.0)],"derivedFrom":[makeQuery(id+"F5.opExtrude","SWEPT_FACE",FACE,{"disambiguationData":[OSD([sQuery(id+"F4.wireOp",EDGE,"E30")])]}),makeQuery(id+"F8.opExtrude","SWEPT_FACE",FACE,{"disambiguationData":[OSD([sQuery(id+"F7.wireOp",EDGE,"E67")])]})]});
            fillet(context, id + "F14", {"entities" : qUnion([Q0, Q1, Q2, Q3, Q4, Q5]), "radius" : 3 * mm, "tangentPropagation" : true, "allowEdgeOverflow" : false});
        }
        {
            var Q0;
            Q0=makeQuery(id+"F1.opExtrude","CAP_EDGE",EDGE,{"disambiguationData":[OSD([sQuery(id+"F0.wireOp",EDGE,"E1.bottom")])],"isStart":false});
            fillet(context, id + "F15", {"entities" : qUnion([Q0]), "radius" : 2 * mm, "tangentPropagation" : true, "allowEdgeOverflow" : false});
        }
        {
            var Q0;
            {var subQ0=sQuery(id+"F0.wireOp",EDGE,"E22.filletArc");var subQ1=sQuery(id+"F0.wireOp",EDGE,"E7");var subQ2=sQuery(id+"F0.wireOp",EDGE,"E6");var subQ3=sQuery(id+"F0.wireOp",EDGE,"E5");var subQ4=sQuery(id+"F0.wireOp",EDGE,"E4");var subQ5=sQuery(id+"F0.wireOp",EDGE,"E1.bottom");var subQ6=sQuery(id+"F0.wireOp",EDGE,"E21.filletArc");var subQ7=sQuery(id+"F0.wireOp",EDGE,"E1.top");var subQ8=sQuery(id+"F0.wireOp",EDGE,"E1.left");var subQ9=sQuery(id+"F0.wireOp",EDGE,"E1.right");var subQ10=sQuery(id+"F0.wireOp",EDGE,"E23.filletArc");var subQ11=sQuery(id+"F0.wireOp",EDGE,"E24.filletArc");Q0=makeQuery(id+"F2.boolean.opBoolean","SPLIT",FACE,{"disambiguationData":[TD([makeQuery(id+"F1.opExtrude","SWEPT_FACE",FACE,{"disambiguationData":[OSD([subQ5])]})])],"derivedFrom":makeQuery(id+"F1.opExtrude","CAP_FACE",FACE,{"disambiguationData":[OSD([subQ5,subQ7,subQ8,subQ9,subQ4,subQ3,subQ2,subQ1,subQ6,subQ0,subQ10,subQ11])],"isStart":true})});}
            var sketch = newSketch(context, id + "F16", { "sketchPlane" : qUnion([Q0])});
            skLineSegment(sketch, "E79", {"start": v(0, -74.25) * mm, "end": v(0, -104.25) * mm, "construction": true});
            skPoint(sketch, "E79.endSnap0", {"position": v(0, -74.25) * mm});
            skCircle(sketch, "E80", {"center": v(0, -104.25) * mm, "radius": 6 * mm});
            skArc(sketch, "E81", {"start": v(15, -104.25) * mm, "mid": v(0, -119.25) * mm, "end": v(-15, -104.25) * mm});
            skLineSegment(sketch, "E82", {"start": v(-15, -104.25) * mm, "end": v(-15, -92.25) * mm});
            skLineSegment(sketch, "E83", {"start": v(15, -104.25) * mm, "end": v(15, -92.25) * mm});
            skLineSegment(sketch, "E84", {"start": v(15, -92.25) * mm, "end": v(33, -74.25) * mm});
            skLineSegment(sketch, "E85", {"start": v(-15, -92.25) * mm, "end": v(-33, -74.25) * mm});
            skLineSegment(sketch, "E86", {"start": v(-74.25, 0) * mm, "end": v(74.25, 0) * mm, "construction": true});
            skSolve(sketch);
        }
    });
